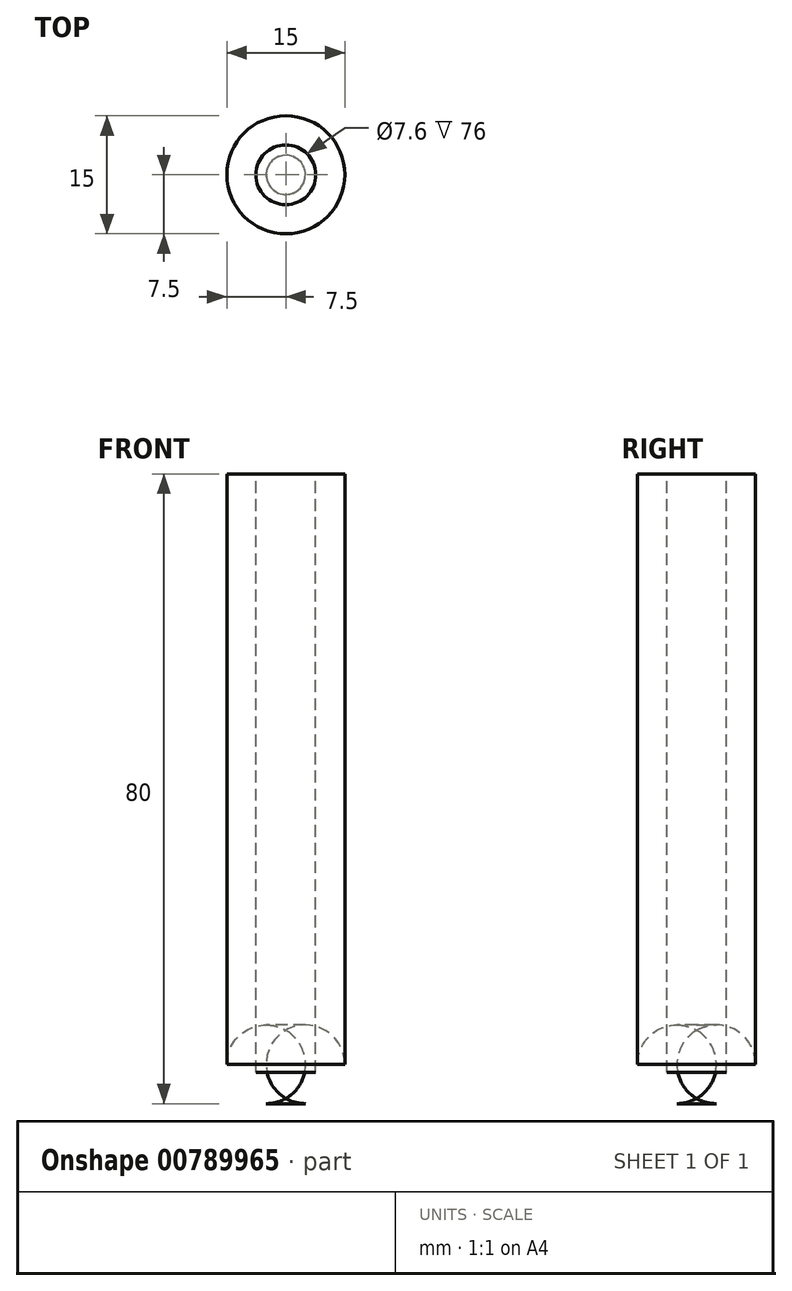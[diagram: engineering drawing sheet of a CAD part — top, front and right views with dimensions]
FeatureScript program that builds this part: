
annotation { "Feature Type Name" : "Feature", "Feature Type Description" : "" }
export const myFeature = defineFeature(function(context is Context, id is Id, definition is map)
    precondition{}
    {
        {
            var Q0;
            Q0=qCreatedBy(makeId("Top.planeOp"),FACE);
            var sketch = newSketch(context, id + "F0", { "sketchPlane" : qUnion([Q0])});
            skCircle(sketch, "E0", {"center": v(0, 0) * mm, "radius": 7.5 * mm});
            skSolve(sketch);
        }
        {
            var Q0;
            Q0=makeQuery(id+"F0.imprint","IMPRINT",FACE,{"disambiguationData":[TD([[makeQuery(id+"F0.imprint","IMPRINT",EDGE,{"derivedFrom":sQuery(id+"F0.wireOp",EDGE,"E0")}),1.0]])]});
            extrude(context, id + "F1", {"entities" : qUnion([Q0]), "depth" : 80 * mm, "offsetDistance" : 25 * mm});
        }
        {
            var Q0;
            Q0=makeQuery(id+"F1.opExtrude","CAP_FACE",FACE,{"disambiguationData":[OSD([sQuery(id+"F0.wireOp",EDGE,"E0")])],"isStart":false});
            var sketch = newSketch(context, id + "F2", { "sketchPlane" : qUnion([Q0])});
            skCircle(sketch, "E1", {"center": v(0, 0) * mm, "radius": 3.8 * mm});
            skSolve(sketch);
        }
        {
            var Q0;
            Q0=makeQuery(id+"F2.imprint","IMPRINT",FACE,{"disambiguationData":[TD([[makeQuery(id+"F2.imprint","IMPRINT",EDGE,{"derivedFrom":sQuery(id+"F2.wireOp",EDGE,"E1")}),1.0]])]});
            extrude(context, id + "F3", {"entities" : qUnion([Q0]), "operationType" : NewBodyOperationType.REMOVE, "oppositeDirection" : true, "depth" : 76 * mm, "offsetDistance" : 25 * mm});
        }
        {
            var Q0;
            Q0=makeQuery(id+"F1.opExtrude","CAP_FACE",FACE,{"disambiguationData":[OSD([sQuery(id+"F0.wireOp",EDGE,"E0")])],"isStart":true});
            fillet(context, id + "F4", {"entities" : qUnion([Q0]), "radius" : 5 * mm, "tangentPropagation" : true, "allowEdgeOverflow" : false});
        }
    });
